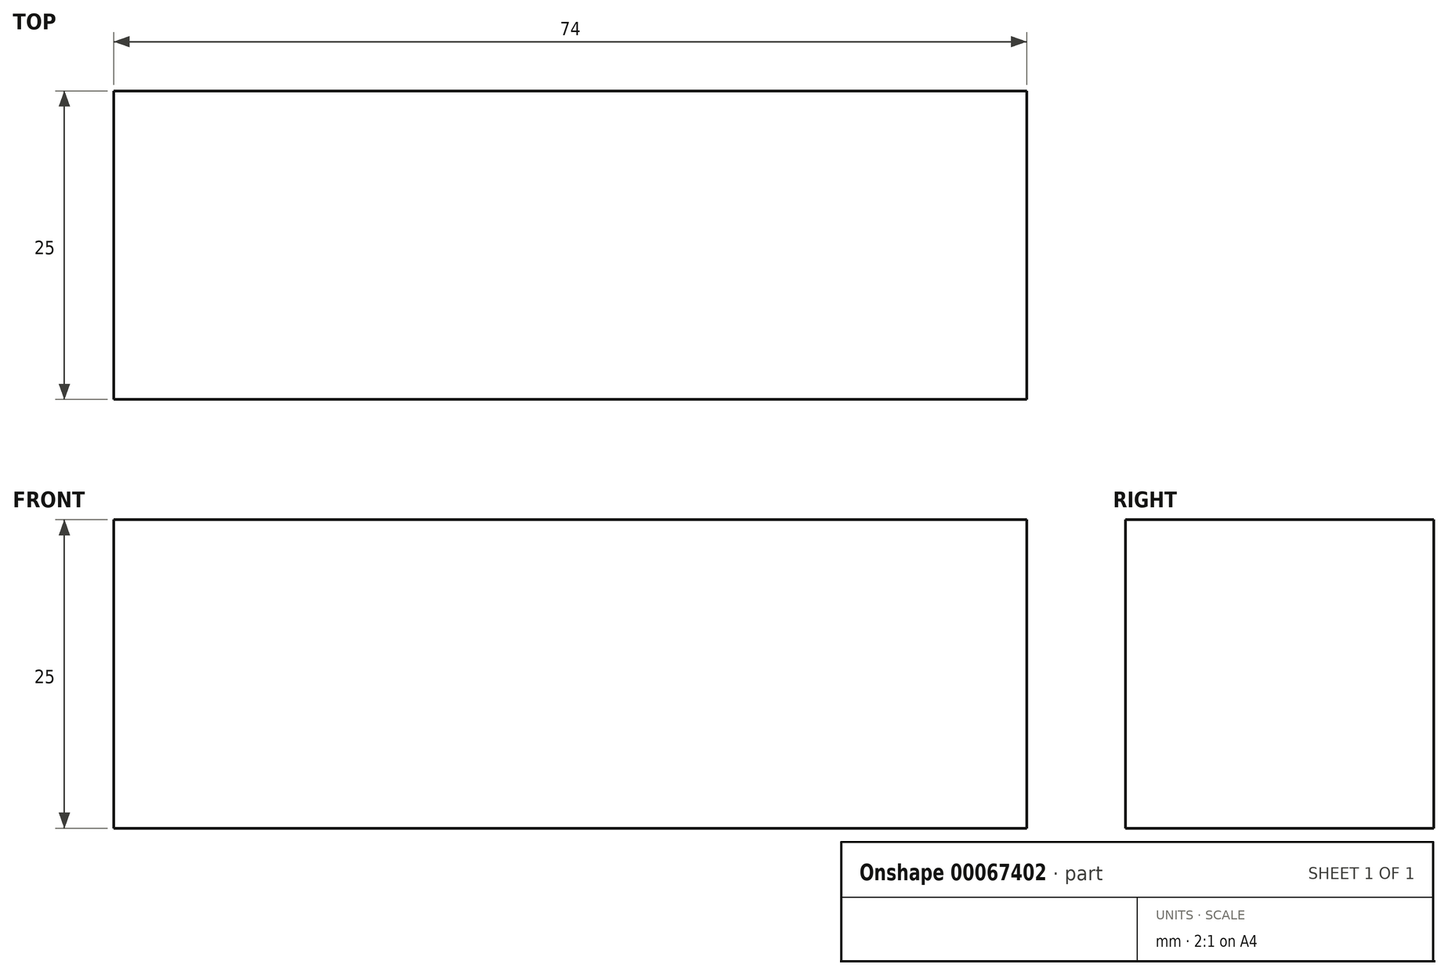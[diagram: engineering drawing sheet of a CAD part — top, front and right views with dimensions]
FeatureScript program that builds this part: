
annotation { "Feature Type Name" : "Feature", "Feature Type Description" : "" }
export const myFeature = defineFeature(function(context is Context, id is Id, definition is map)
    precondition{}
    {
        {
            var Q0;
            Q0=qCreatedBy(makeId("Top.planeOp"),FACE);
            var sketch = newSketch(context, id + "F0", { "sketchPlane" : qUnion([Q0])});
            skLineSegment(sketch, "E0.bottom", {"start": v(37, 12.5) * mm, "end": v(-37, 12.5) * mm});
            skLineSegment(sketch, "E0.top", {"start": v(37, -12.5) * mm, "end": v(-37, -12.5) * mm});
            skLineSegment(sketch, "E0.left", {"start": v(37, 12.5) * mm, "end": v(37, -12.5) * mm});
            skLineSegment(sketch, "E0.right", {"start": v(-37, 12.5) * mm, "end": v(-37, -12.5) * mm});
            skPoint(sketch, "E0.middle", {"position": v(0, 0) * mm});
            skSolve(sketch);
        }
        {
            var Q0;
            Q0 = qSketchRegion(id + "F0", true);
            extrude(context, id + "F1", {"entities" : qUnion([Q0]), "endBound" : BoundingType.SYMMETRIC, "depth" : 25 * mm});
        }
    });
